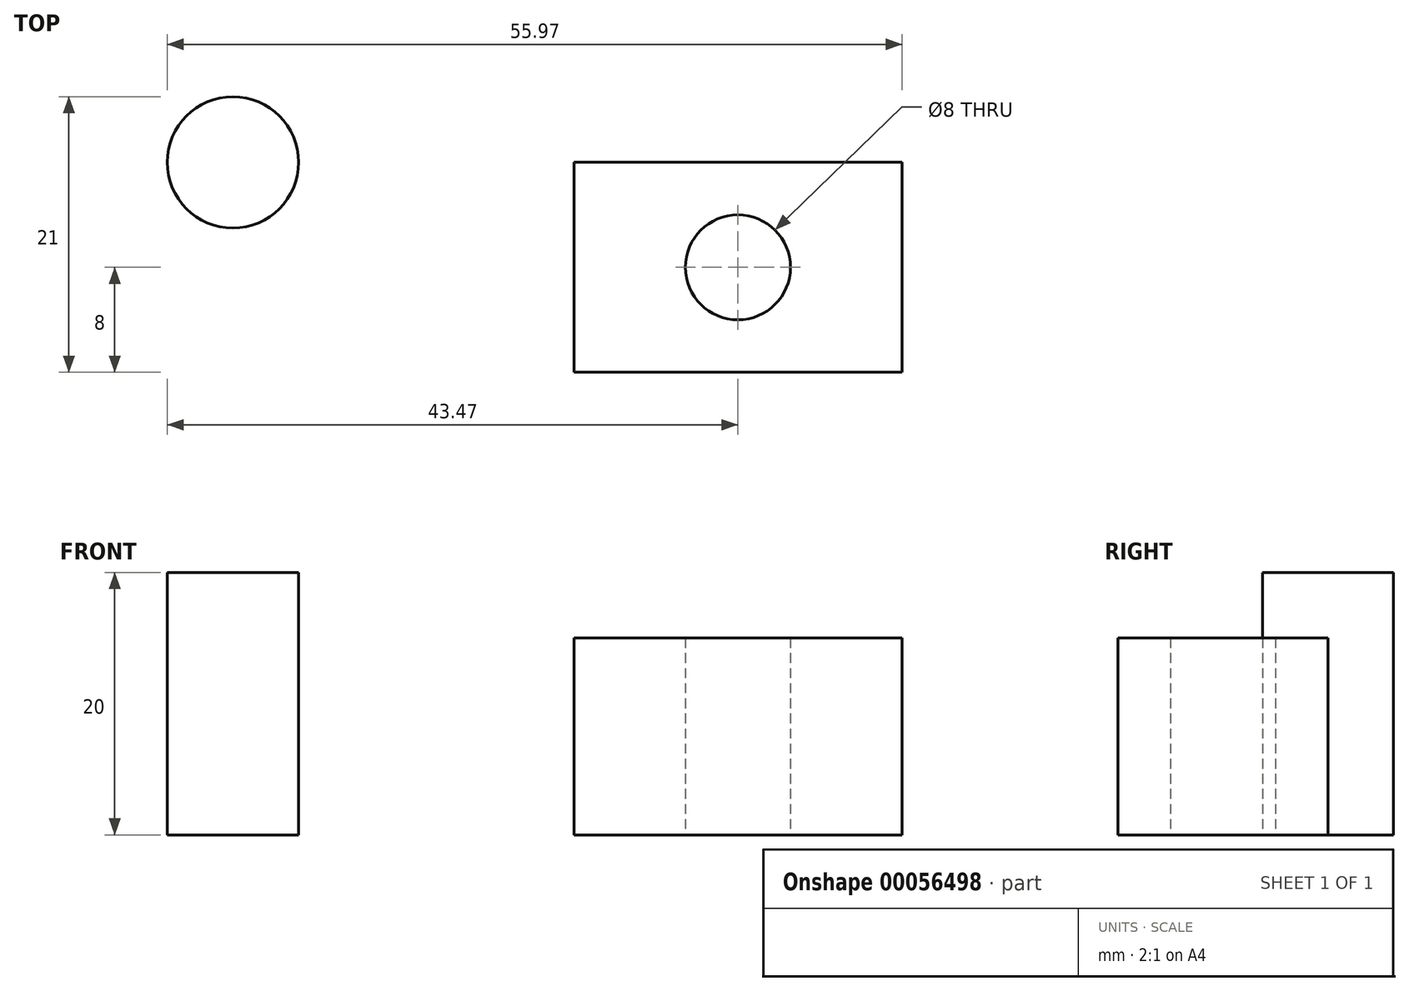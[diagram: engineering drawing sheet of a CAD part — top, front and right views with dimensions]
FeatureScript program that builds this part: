
annotation { "Feature Type Name" : "Feature", "Feature Type Description" : "" }
export const myFeature = defineFeature(function(context is Context, id is Id, definition is map)
    precondition{}
    {
        {
            var Q0;
            Q0=qCreatedBy(makeId("Top.planeOp"),FACE);
            var sketch = newSketch(context, id + "F0", { "sketchPlane" : qUnion([Q0])});
            skLineSegment(sketch, "E0.bottom", {"start": v(0, 0) * mm, "end": v(25, 0) * mm});
            skLineSegment(sketch, "E0.top", {"start": v(0, -16) * mm, "end": v(25, -16) * mm});
            skLineSegment(sketch, "E0.left", {"start": v(0, 0) * mm, "end": v(0, -16) * mm});
            skLineSegment(sketch, "E0.right", {"start": v(25, 0) * mm, "end": v(25, -16) * mm});
            skLineSegment(sketch, "E1", {"start": v(0, 0) * mm, "end": v(25, -16) * mm, "construction": true});
            skCircle(sketch, "E2", {"center": v(12.5, -8) * mm, "radius": 4 * mm});
            skSolve(sketch);
        }
        {
            var Q0;
            Q0=makeQuery(id+"F0.imprint","IMPRINT",FACE,{"disambiguationData":[TD([[makeQuery(id+"F0.imprint","IMPRINT",EDGE,{"derivedFrom":sQuery(id+"F0.wireOp",EDGE,"E0.bottom")}),-1.0]])]});
            extrude(context, id + "F1", {"entities" : qUnion([Q0]), "depth" : 15 * mm});
        }
        {
            var Q0;
            Q0=qCreatedBy(makeId("Top.planeOp"),FACE);
            var sketch = newSketch(context, id + "F2", { "sketchPlane" : qUnion([Q0])});
            skLineSegment(sketch, "E3", {"start": v(0, 0) * mm, "end": v(-25.97, 0) * mm});
            skCircle(sketch, "E4", {"center": v(-25.97, 0) * mm, "radius": 5 * mm});
            skSolve(sketch);
        }
        {
            var Q0;
            Q0=makeQuery(id+"F2.imprint","IMPRINT",FACE,{"disambiguationData":[TD([[makeQuery(id+"F2.imprint","IMPRINT",EDGE,{"derivedFrom":sQuery(id+"F2.wireOp",EDGE,"E4")}),1.0]])]});
            extrude(context, id + "F3", {"entities" : qUnion([Q0]), "depth" : 20 * mm});
        }
    });
